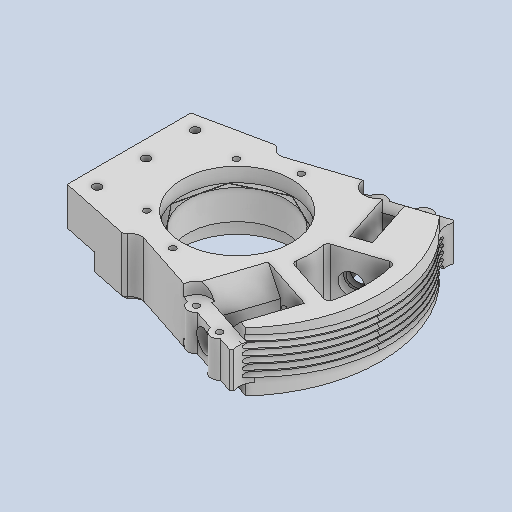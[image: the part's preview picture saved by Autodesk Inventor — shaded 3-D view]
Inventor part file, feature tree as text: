
AUTODESK INVENTOR PART (.ipt)
format: ipt  version: 2025.2 (Build 292293000, 293)  size: 1,026,560 bytes
history: native  units: mm
features: sketch x39, extrude x33, helix x12, projected_geometry x4, chamfer x3, other x2, fillet x2, plane x1
ambient origin geometry x8: Origin, YZ Plane, XZ Plane, XY Plane, X Axis, Y Axis, Z Axis, Center Point
bodies: Solid1 (feature_tree)
feature tree (96):
  other  "Big_drum"
  extrude  "Extrusion1"  Depth=28.0mm TaperAngle=0.0deg
  sketch  "Sketch2"  dims[d7=8.5mm d9=60.0deg]
  extrude  "Extrusion2"  Depth=70.0mm
  extrude  "Extrusion3"  TaperAngle=60.0deg  [1 undecoded]
  extrude  "Extrusion4"  TaperAngle=0.0deg  [1 undecoded]
  extrude  "Extrusion5"  Depth=10.0mm
  extrude  "Extrusion6"  TaperAngle=0.0deg  [1 undecoded]
  extrude  "Extrusion7"  Depth=7.0mm TaperAngle=0.0deg
  extrude  "Extrusion8"  Depth=7.0mm TaperAngle=0.0deg
  extrude  "Extrusion9"  Depth=7.0mm
  fillet  "Fillet1"  Radius=7.0mm
  extrude  "Extrusion10"  TaperAngle=0.0deg  [1 undecoded]
  extrude  "Extrusion11"  Depth=7.0mm
  extrude  "Extrusion12"  Depth=7.0mm
  extrude  "Extrusion13"  Depth=2.0mm
  chamfer  "Chamfer3"  Distance=5.5mm
  extrude  "Extrusion14"  Depth=5.5mm TaperAngle=0.0deg
  extrude  "Extrusion15"  Depth=5.5mm TaperAngle=0.0deg
  extrude  "Extrusion16"  Depth=2.0mm
  extrude  "Extrusion17"  Depth=4.0mm TaperAngle=0.0deg
  extrude  "Extrusion18"  TaperAngle=0.0deg  [1 undecoded]
  extrude  "Extrusion19"  Depth=4.0mm TaperAngle=0.0deg
  chamfer  "Chamfer4"  Distance=10.0mm
  extrude  "Extrusion20"  Depth=5.5mm TaperAngle=0.0deg
  extrude  "Extrusion21"  Depth=10.0mm TaperAngle=0.0deg
  sketch  "Sketch23"  dims[d76=5.1mm]
  extrude  "Extrusion22"  Depth=3.0mm
  extrude  "Extrusion23"  Depth=3.0mm
  extrude  "Extrusion24"  TaperAngle=0.0deg  [1 undecoded]
  extrude  "Extrusion25"  Depth=4.0mm
  plane  "Work Plane1"
  sketch  "Sketch29"  dims[d89=3.0mm d90=3.0mm]
  helix  "Coil2"  [1 undecoded]
  helix  "Coil3"  [1 undecoded]
  sketch  "Sketch30"  dims[d91=3.0mm d92=3.0mm]
  helix  "Coil4"  [1 undecoded]
  helix  "Coil5"  [1 undecoded]
  helix  "Coil6"  [1 undecoded]
  helix  "Coil7"  [1 undecoded]
  helix  "Coil8"  [1 undecoded]
  helix  "Coil9"  [1 undecoded]
  helix  "Coil10"  [1 undecoded]
  helix  "Coil11"  [1 undecoded]
  helix  "Coil12"  [1 undecoded]
  helix  "Coil13"  [1 undecoded]
  extrude  "Extrusion26"  Depth=5.0mm
  extrude  "Extrusion27"  Depth=10.0mm
  sketch  "Sketch35"  dims[d133=24.0mm d134=30.75mm d135=5.0mm d136=0.0mm d137=90.0deg d138=90.0deg d139=0.0mm d140=0.0mm d141=5.625mm d142=2.5mm]
  extrude  "Extrusion28"  Depth=10.0mm TaperAngle=0.0deg
  extrude  "Extrusion29"  Depth=0.75mm TaperAngle=0.0deg
  extrude  "Extrusion30"  Depth=0.5mm
  sketch  "Sketch41"  dims[d168=24.0mm d169=27.25mm d170=5.0mm d171=0.0mm d172=90.0deg d173=90.0deg d174=0.0mm d175=0.0mm]
  extrude  "Extrusion31"  Depth=18.0mm TaperAngle=0.0deg
  extrude  "Extrusion32"  Depth=18.0mm TaperAngle=0.0deg
  fillet  "Fillet2"  Radius=4.0mm
  extrude  "Extrusion33"  Depth=4.0mm
  chamfer  "Chamfer6"  Distance=12.0mm
  sketch  "Sketch1"  dims[d0=136.0mm d1=28.0mm d2=0.0mm]
  sketch  "Sketch3"  dims[d10=1.22173mm d11=0.0mm d12=0.0mm]
  sketch  "Sketch4"  dims[d13=10.0mm d14=0.0mm d15=50.0mm]
  sketch  "Sketch6"  dims[d17=1.5mm d18=0.0mm d19=0.0mm]
  sketch  "Sketch7"  dims[d20=52.1mm d21=7.0mm d22=0.0mm]
  sketch  "Sketch8"  dims[d23=7.0mm d24=0.0mm d25=14.2mm d26=0.0mm]
  sketch  "Sketch9"  dims[d27=8.5mm d28=14.75mm d30=7.0mm]
  sketch  "Sketch10"  dims[d31=24.0mm d32=0.0mm d33=0.0mm]
  sketch  "Sketch11"  dims[d36=7.0mm d37=7.0mm]
  sketch  "Sketch12"  dims[d38=7.0mm d39=9.0mm]
  sketch  "Sketch13"  dims[d40=0.0mm d41=0.0mm d42=2.0mm]
  sketch  "Sketch15"  dims[d43=8.0mm d44=5.5mm d45=0.0mm]
  sketch  "Sketch16"  dims[d49=8.0mm d50=5.5mm d51=0.0mm]
  sketch  "Sketch17"  dims[d55=5.5mm d56=0.0mm d57=5.5mm d58=0.0mm]
  sketch  "Sketch18"  dims[d61=3.75mm d62=2.0mm d63=45.0deg d64=8.0mm]
  sketch  "Sketch19"  dims[d65=10.2mm d66=4.0mm d67=0.0mm]
  sketch  "Sketch20"  dims[d68=1.0mm d69=0.0mm d70=0.0mm]
  sketch  "Sketch21"  dims[d71=4.0mm d72=0.0mm d73=4.0mm d74=0.0mm]
  sketch  "Sketch22"  dims[d75=3.0mm]
  sketch  "Sketch24"  dims[d77=2.0mm]
  sketch  "Sketch25"  dims[d78=2.5mm d79=10.0mm d80=0.0mm]
  sketch  "Sketch26"  dims[d81=2.5mm d82=5.5mm d83=0.0mm]
  sketch  "Sketch27"  dims[d84=5.5mm d85=2.0mm d86=45.0deg d87=10.0mm d88=0.0mm]
  other  "Work Axis1"
  sketch  "Sketch31"  dims[d93=0.0mm d94=0.0mm d95=0.0mm d96=0.0mm]
  projected_geometry  "Projected Loop1"
  sketch  "Sketch Rectangular Pattern1"  dims[d3=6.981317mm d5=70.0mm]
  sketch  "Sketch32"  dims[d97=10.2mm d98=4.25mm d99=4.25mm d100=8.5mm d101=8.5mm d102=5.0mm d103=4.0mm d104=0.0mm d105=0.0mm d106=1.0mm d107=5.0mm d108=0.0mm d109=4.0mm d110=0.0mm d111=-7.679449mm d123=4.875mm d124=2.5mm]
  projected_geometry  "Projected Loop2"
  projected_geometry  "Projected Loop3"
  sketch  "Sketch34"  dims[d125=24.0mm d126=30.75mm d127=10.0mm d128=0.0mm d129=90.0deg d130=90.0deg d131=0.0mm d132=0.0mm]
  sketch  "Sketch36"  dims[d143=24.0mm d144=30.75mm d145=5.0mm d146=0.0mm d147=90.0deg d148=90.0deg d149=0.0mm d150=0.0mm]
  sketch  "Sketch37"  dims[d151=24.0mm d152=30.75mm d153=5.0mm d154=0.0mm d155=90.0deg d156=90.0deg d157=0.0mm d158=0.0mm d159=4.875mm]
  sketch  "Sketch38"  dims[d160=2.5mm d161=50.0mm d163=3.0mm d164=10.0mm d166=10.0mm]
  projected_geometry  "Projected Loop5"
  sketch  "Sketch42"  dims[d176=24.0mm d177=27.25mm d178=5.0mm d179=0.0mm d180=90.0deg d181=90.0deg d182=0.0mm d183=0.0mm]
  sketch  "Sketch43"  dims[d184=24.0mm d185=27.25mm d186=5.0mm d187=0.0mm d188=90.0deg d189=90.0deg d190=0.0mm d191=0.0mm]
  sketch  "Sketch44"  dims[d192=24.0mm d193=27.25mm d194=5.0mm d195=0.0mm d196=90.0deg d197=90.0deg d198=0.0mm d199=0.0mm d200=24.0mm d201=27.25mm d202=5.0mm d203=0.0mm d204=90.0deg d205=90.0deg d206=0.0mm d207=0.0mm d208=24.0mm d209=27.25mm d210=5.0mm d211=0.0mm d212=90.0deg d213=90.0deg d214=0.0mm d215=0.0mm d216=24.0mm d217=27.25mm d218=5.0mm d219=0.0mm d220=90.0deg d221=90.0deg d222=0.0mm d223=0.0mm d224=24.0mm d225=27.25mm d226=5.0mm d227=0.0mm d228=90.0deg d229=90.0deg d230=0.0mm d231=0.0mm d232=10.0mm d233=0.0mm d234=0.75mm d235=0.0mm d236=40.0mm d237=18.0mm d238=0.0mm d239=18.0mm d240=0.0mm d241=4.0mm d242=4.0mm d244=12.0mm d245=3.0mm d246=3.0mm d247=18.5mm d248=0.0mm d250=150.0mm d251=38.0mm d253=5.0mm d254=10.0mm d255=0.0mm d256=10.0mm d257=0.0mm d258=2.0mm d259=4.0mm d260=31.027281mm d261=7.75682mm d262=0.0mm d263=0.0mm d264=17.0mm d268=2.0mm d269=2.0mm d270=45.0deg d59=0.5mm d60=0.872665mm d249=0.5mm d252=0.872665mm]
note: 18 required parameter values undecoded (feature->parameter linkage not recoverable at this tier; creation-order binding heuristic only, values carry confidence <= 0.55)
